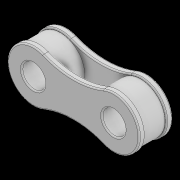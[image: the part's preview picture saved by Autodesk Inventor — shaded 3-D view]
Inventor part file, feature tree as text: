
AUTODESK INVENTOR PART (.ipt)
format: ipt  version: 2021 (Build 250183000, 183)  size: 217,600 bytes
history: native  units: in
note: dims shown in document units (in); Inventor stores cm internally (conversion verified against a paired STEP export)
features: extrude x2, sketch x2, plane x1, mirror x1, fillet x1
ambient origin geometry x8: Origin, YZ Plane, XZ Plane, XY Plane, X Axis, Y Axis, Z Axis, Center Point
bodies: Solid1 (feature_tree)
feature tree (7):
  plane  "Work Plane1"
  extrude  "Extrusion1"  Depth=0.1441in
  mirror  "Mirror1"
  extrude  "Extrusion2"  Depth=0.0079in
  fillet  "Fillet1"  Radius=0.5in
  sketch  "Sketch1"  dims[d1=0.3051in d2=0.1441in]
  sketch  "Sketch2"  dims[d0=0.065in d3=0.3228in d4=0.5in d5=0.4921in d6=0.1441in d7=0.0394in d8=0.0in d9=0.3051in d10=0.1299in d11=0.0in d12=0.0079in]
